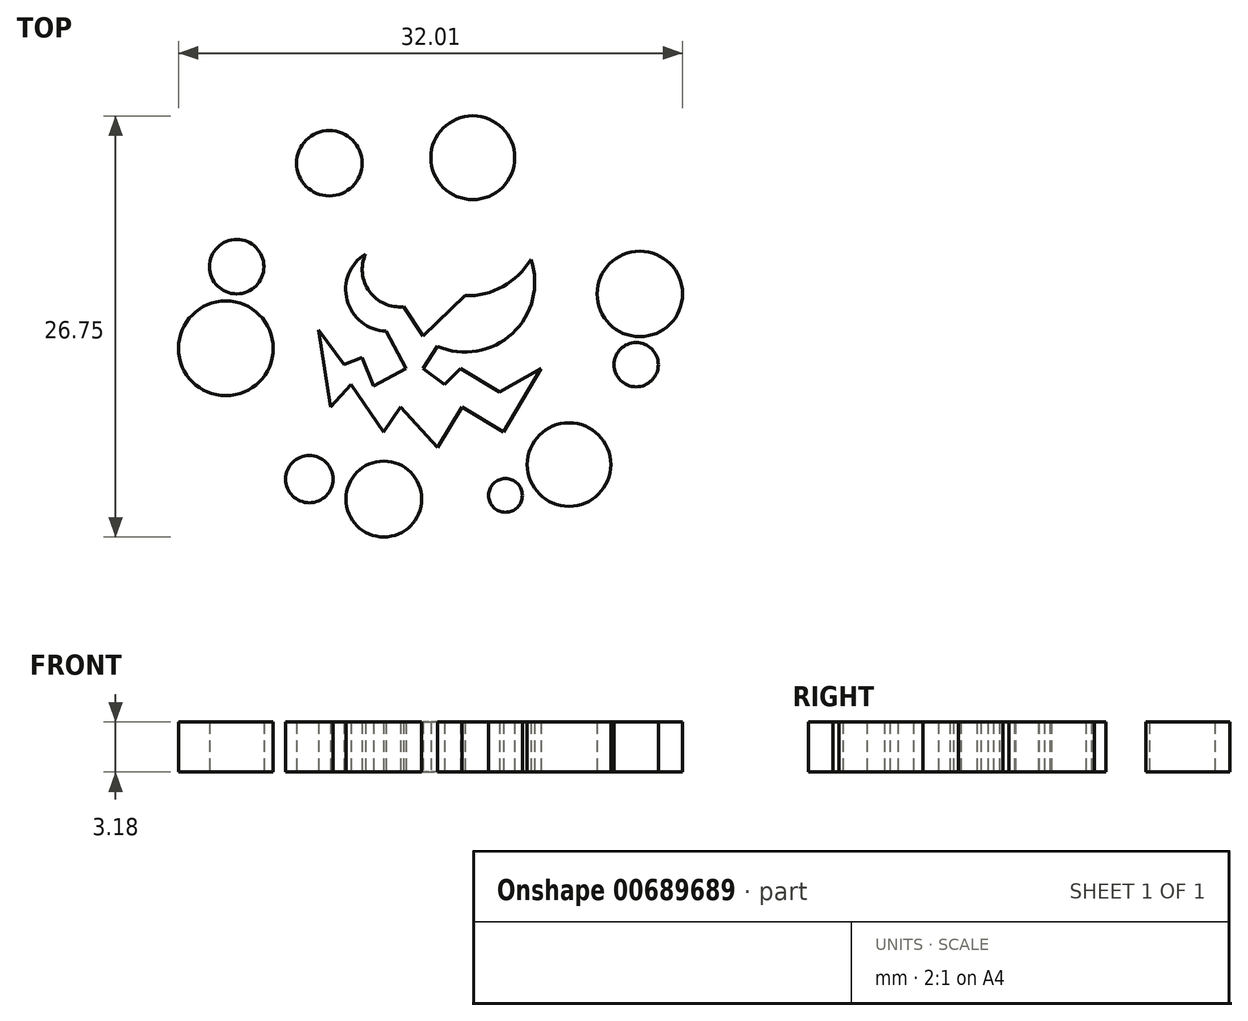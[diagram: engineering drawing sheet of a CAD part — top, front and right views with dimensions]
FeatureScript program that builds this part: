
annotation { "Feature Type Name" : "Feature", "Feature Type Description" : "" }
export const myFeature = defineFeature(function(context is Context, id is Id, definition is map)
    precondition{}
    {
        {
            var Q0;
            Q0=qCreatedBy(makeId("Top.planeOp"),FACE);
            var sketch = newSketch(context, id + "F0", { "sketchPlane" : qUnion([Q0])});
            skCircle(sketch, "E0", {"center": v(2.07, 12.3) * mm, "radius": 2.66 * mm});
            skCircle(sketch, "E1", {"center": v(-7.04, 11.96) * mm, "radius": 2.08 * mm});
            skCircle(sketch, "E2", {"center": v(-12.92, 5.4) * mm, "radius": 1.73 * mm});
            skCircle(sketch, "E3", {"center": v(-13.62, 0.2) * mm, "radius": 3 * mm});
            skCircle(sketch, "E4", {"center": v(-8.31, -8.1) * mm, "radius": 1.5 * mm});
            skCircle(sketch, "E5", {"center": v(-3.58, -9.37) * mm, "radius": 2.4 * mm});
            skCircle(sketch, "E6", {"center": v(4.14, -9.14) * mm, "radius": 1.07 * mm});
            skCircle(sketch, "E7", {"center": v(8.18, -7.18) * mm, "radius": 2.65 * mm});
            skCircle(sketch, "E8", {"center": v(12.45, -0.84) * mm, "radius": 1.4 * mm});
            skCircle(sketch, "E9", {"center": v(12.68, 3.66) * mm, "radius": 2.71 * mm});
            skLineSegment(sketch, "E10", {"start": v(-7.73, 1.35) * mm, "end": v(-6.96, -3.52) * mm});
            skLineSegment(sketch, "E11", {"start": v(-6.96, -3.52) * mm, "end": v(-5.66, -2.1) * mm});
            skLineSegment(sketch, "E12", {"start": v(-5.66, -2.1) * mm, "end": v(-3.6, -5.1) * mm});
            skLineSegment(sketch, "E13", {"start": v(-3.6, -5.1) * mm, "end": v(-2.53, -3.52) * mm});
            skLineSegment(sketch, "E14", {"start": v(-2.53, -3.52) * mm, "end": v(-0.18, -6.1) * mm});
            skLineSegment(sketch, "E15", {"start": v(-0.18, -6.1) * mm, "end": v(1.38, -3.52) * mm});
            skLineSegment(sketch, "E16", {"start": v(1.38, -3.52) * mm, "end": v(4.01, -5.1) * mm});
            skLineSegment(sketch, "E17", {"start": v(4.01, -5.1) * mm, "end": v(6.42, -1.1) * mm});
            skLineSegment(sketch, "E18", {"start": v(6.42, -1.1) * mm, "end": v(3.76, -2.56) * mm});
            skLineSegment(sketch, "E19", {"start": v(3.76, -2.56) * mm, "end": v(1.3, -1.1) * mm});
            skLineSegment(sketch, "E20", {"start": v(1.3, -1.1) * mm, "end": v(0.28, -2.1) * mm});
            skLineSegment(sketch, "E21", {"start": v(0.28, -2.1) * mm, "end": v(-1.1, -1.1) * mm});
            skLineSegment(sketch, "E22", {"start": v(-1.1, -1.1) * mm, "end": v(-0.18, 0.33) * mm});
            skLineSegment(sketch, "E23", {"start": v(-7.73, 1.35) * mm, "end": v(-6.12, -0.84) * mm});
            skLineSegment(sketch, "E24", {"start": v(-6.12, -0.84) * mm, "end": v(-4.95, -0.38) * mm});
            skLineSegment(sketch, "E25", {"start": v(-4.95, -0.38) * mm, "end": v(-4.24, -2.18) * mm});
            skLineSegment(sketch, "E26", {"start": v(-4.24, -2.18) * mm, "end": v(-2.18, -1.1) * mm});
            skLineSegment(sketch, "E27", {"start": v(-2.18, -1.1) * mm, "end": v(-3.44, 1.3) * mm});
            skArc(sketch, "E28", {"start": v(-4.74, 6.2) * mm, "mid": v(-5.92, 3.26) * mm, "end": v(-3.44, 1.3) * mm});
            skArc(sketch, "E29", {"start": v(-4.74, 6.2) * mm, "mid": v(-4.5, 3.82) * mm, "end": v(-2.31, 2.85) * mm});
            skArc(sketch, "E30", {"start": v(-0.18, 0.33) * mm, "mid": v(4.6, 1.15) * mm, "end": v(5.76, 5.85) * mm});
            skArc(sketch, "E31", {"start": v(1.58, 3.55) * mm, "mid": v(3.98, 4.13) * mm, "end": v(5.76, 5.85) * mm});
            skLineSegment(sketch, "E32", {"start": v(-2.31, 2.85) * mm, "end": v(-1.1, 0.97) * mm});
            skLineSegment(sketch, "E33", {"start": v(1.58, 3.55) * mm, "end": v(-1.1, 0.97) * mm});
            skSolve(sketch);
        }
        {
            var Q0;
            Q0=makeQuery(id+"F0.imprint","IMPRINT",FACE,{"disambiguationData":[TD([[makeQuery(id+"F0.imprint","IMPRINT",EDGE,{"derivedFrom":sQuery(id+"F0.wireOp",EDGE,"E10")}),1.0]])]});
            var Q1;
            Q1=makeQuery(id+"F0.imprint","IMPRINT",FACE,{"disambiguationData":[TD([[makeQuery(id+"F0.imprint","IMPRINT",EDGE,{"derivedFrom":sQuery(id+"F0.wireOp",EDGE,"E3")}),1.0]])]});
            var Q2;
            Q2=makeQuery(id+"F0.imprint","IMPRINT",FACE,{"disambiguationData":[TD([[makeQuery(id+"F0.imprint","IMPRINT",EDGE,{"derivedFrom":sQuery(id+"F0.wireOp",EDGE,"E2")}),1.0]])]});
            var Q3;
            Q3=makeQuery(id+"F0.imprint","IMPRINT",FACE,{"disambiguationData":[TD([[makeQuery(id+"F0.imprint","IMPRINT",EDGE,{"derivedFrom":sQuery(id+"F0.wireOp",EDGE,"3af36cb1-77a5-494c-97c9-342cf889bdbf")}),1.0]])]});
            var Q4;
            Q4=makeQuery(id+"F0.imprint","IMPRINT",FACE,{"disambiguationData":[TD([[makeQuery(id+"F0.imprint","IMPRINT",EDGE,{"derivedFrom":sQuery(id+"F0.wireOp",EDGE,"E1")}),1.0]])]});
            var Q5;
            Q5=makeQuery(id+"F0.imprint","IMPRINT",FACE,{"disambiguationData":[TD([[makeQuery(id+"F0.imprint","IMPRINT",EDGE,{"derivedFrom":sQuery(id+"F0.wireOp",EDGE,"E0")}),1.0]])]});
            var Q6;
            Q6=makeQuery(id+"F0.imprint","IMPRINT",FACE,{"disambiguationData":[TD([[makeQuery(id+"F0.imprint","IMPRINT",EDGE,{"derivedFrom":sQuery(id+"F0.wireOp",EDGE,"e8eda26f-9e9d-48c6-b36b-d6f15c1cc4fd")}),1.0]])]});
            var Q7;
            Q7=makeQuery(id+"F0.imprint","IMPRINT",FACE,{"disambiguationData":[TD([[makeQuery(id+"F0.imprint","IMPRINT",EDGE,{"derivedFrom":sQuery(id+"F0.wireOp",EDGE,"e6e7f1e5-28a5-4246-92b8-76de65760aa8")}),1.0]])]});
            var Q8;
            Q8=makeQuery(id+"F0.imprint","IMPRINT",FACE,{"disambiguationData":[TD([[makeQuery(id+"F0.imprint","IMPRINT",EDGE,{"derivedFrom":sQuery(id+"F0.wireOp",EDGE,"E9")}),1.0]])]});
            var Q9;
            Q9=makeQuery(id+"F0.imprint","IMPRINT",FACE,{"disambiguationData":[TD([[makeQuery(id+"F0.imprint","IMPRINT",EDGE,{"derivedFrom":sQuery(id+"F0.wireOp",EDGE,"E8")}),1.0]])]});
            var Q10;
            Q10=makeQuery(id+"F0.imprint","IMPRINT",FACE,{"disambiguationData":[TD([[makeQuery(id+"F0.imprint","IMPRINT",EDGE,{"derivedFrom":sQuery(id+"F0.wireOp",EDGE,"6acb9927-c304-472c-9ec3-8c265c019c99")}),1.0]])]});
            var Q11;
            Q11=makeQuery(id+"F0.imprint","IMPRINT",FACE,{"disambiguationData":[TD([[makeQuery(id+"F0.imprint","IMPRINT",EDGE,{"derivedFrom":sQuery(id+"F0.wireOp",EDGE,"E7")}),1.0]])]});
            var Q12;
            Q12=makeQuery(id+"F0.imprint","IMPRINT",FACE,{"disambiguationData":[TD([[makeQuery(id+"F0.imprint","IMPRINT",EDGE,{"derivedFrom":sQuery(id+"F0.wireOp",EDGE,"E6")}),1.0]])]});
            var Q13;
            Q13=makeQuery(id+"F0.imprint","IMPRINT",FACE,{"disambiguationData":[TD([[makeQuery(id+"F0.imprint","IMPRINT",EDGE,{"derivedFrom":sQuery(id+"F0.wireOp",EDGE,"E5")}),1.0]])]});
            var Q14;
            Q14=makeQuery(id+"F0.imprint","IMPRINT",FACE,{"disambiguationData":[TD([[makeQuery(id+"F0.imprint","IMPRINT",EDGE,{"derivedFrom":sQuery(id+"F0.wireOp",EDGE,"E4")}),1.0]])]});
            var Q15;
            Q15=makeQuery(id+"F0.imprint","IMPRINT",FACE,{"disambiguationData":[TD([[makeQuery(id+"F0.imprint","IMPRINT",EDGE,{"derivedFrom":sQuery(id+"F0.wireOp",EDGE,"eff033ba-6394-4e3c-9b16-d84409a81c1f")}),1.0]])]});
            extrude(context, id + "F1", {"entities" : qUnion([Q0, Q1, Q2, Q3, Q4, Q5, Q6, Q7, Q8, Q9, Q10, Q11, Q12, Q13, Q14, Q15]), "depth" : 3.17 * mm, "offsetDistance" : 25.4 * mm});
        }
    });
